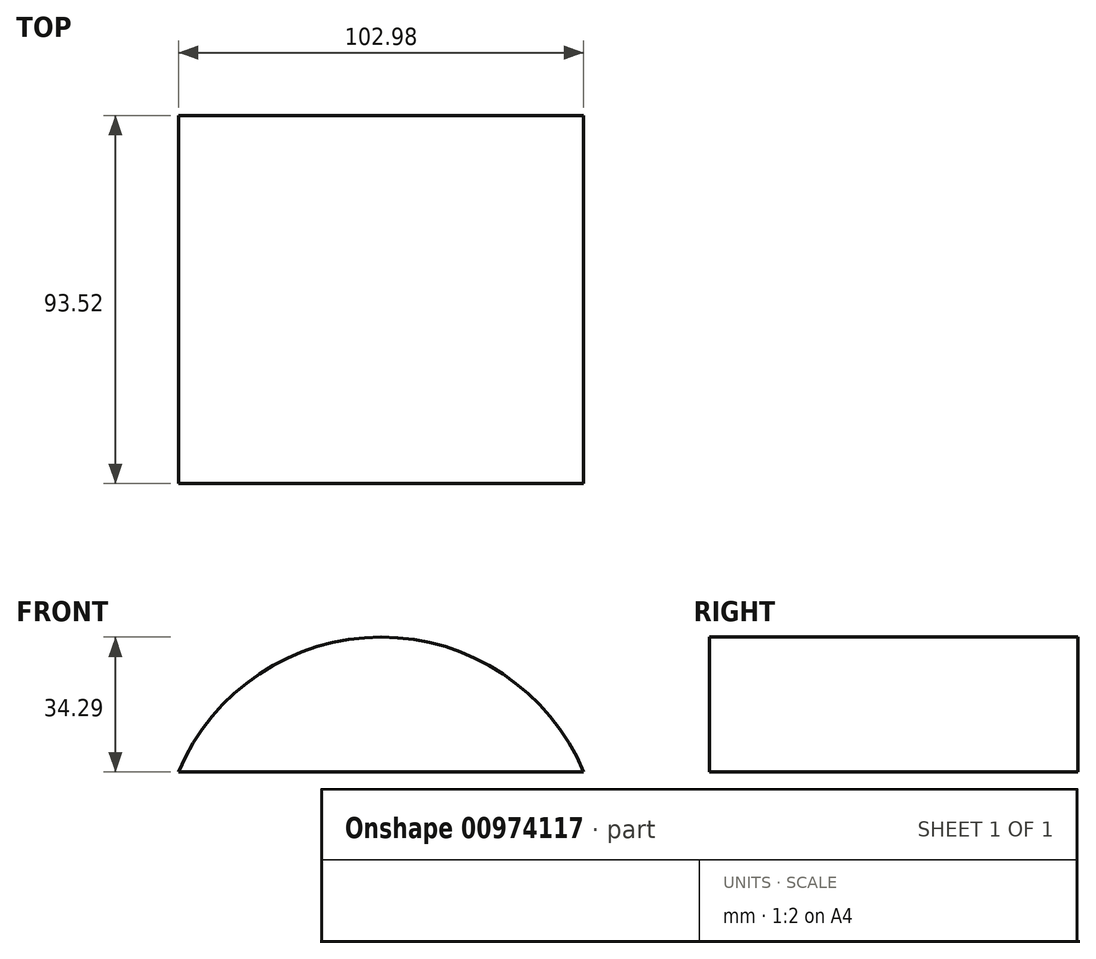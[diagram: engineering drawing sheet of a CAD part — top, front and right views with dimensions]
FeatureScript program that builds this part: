
annotation { "Feature Type Name" : "Feature", "Feature Type Description" : "" }
export const myFeature = defineFeature(function(context is Context, id is Id, definition is map)
    precondition{}
    {
        {
            var Q0;
            Q0=qCreatedBy(makeId("Top.planeOp"),FACE);
            var sketch = newSketch(context, id + "F0", { "sketchPlane" : qUnion([Q0])});
            skLineSegment(sketch, "E0.bottom", {"start": v(-44.18, 41.51) * mm, "end": v(58.8, 41.51) * mm});
            skLineSegment(sketch, "E0.top", {"start": v(-44.18, -52.01) * mm, "end": v(58.8, -52.01) * mm});
            skLineSegment(sketch, "E0.left", {"start": v(-44.18, 41.51) * mm, "end": v(-44.18, -52.01) * mm});
            skLineSegment(sketch, "E0.right", {"start": v(58.8, 41.51) * mm, "end": v(58.8, -52.01) * mm});
            skSolve(sketch);
        }
        {
            var Q0;
            Q0=makeQuery(id+"F0.imprint","IMPRINT",FACE,{"disambiguationData":[TD([[makeQuery(id+"F0.imprint","IMPRINT",EDGE,{"derivedFrom":sQuery(id+"F0.wireOp",EDGE,"E0.bottom")}),-1.0]])]});
            extrude(context, id + "F1", {"entities" : qUnion([Q0]), "depth" : 80.7 * mm, "offsetDistance" : 25.4 * mm});
        }
        {
            var Q0;
            Q0=makeQuery(id+"F1.opExtrude","SWEPT_FACE",FACE,{"disambiguationData":[OSD([sQuery(id+"F0.wireOp",EDGE,"E0.top")])]});
            var sketch = newSketch(context, id + "F2", { "sketchPlane" : qUnion([Q0])});
            skArc(sketch, "E1", {"start": v(58.8, 0) * mm, "mid": v(7.31, 34.29) * mm, "end": v(-44.18, 0) * mm});
            skSolve(sketch);
        }
        {
            var Q0;
            Q0=makeQuery(id+"F2.imprint","IMPRINT",FACE,{"disambiguationData":[TD([[makeQuery(id+"F2.imprint","IMPRINT",EDGE,{"derivedFrom":sQuery(id+"F2.wireOp",EDGE,"E1")}),1.0]])]});
            extrude(context, id + "F3", {"entities" : qUnion([Q0]), "operationType" : NewBodyOperationType.INTERSECT, "oppositeDirection" : true, "depth" : 127.06 * mm, "offsetDistance" : 25.4 * mm});
        }
    });
